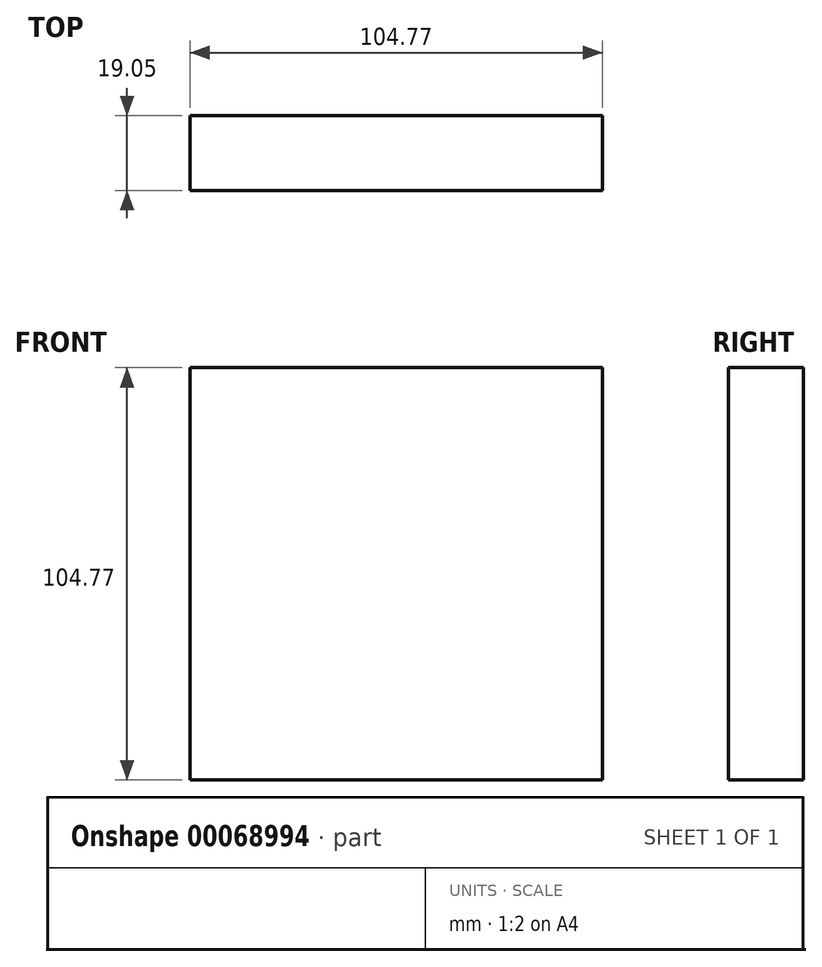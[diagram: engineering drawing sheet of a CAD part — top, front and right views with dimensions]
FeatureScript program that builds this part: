
annotation { "Feature Type Name" : "Feature", "Feature Type Description" : "" }
export const myFeature = defineFeature(function(context is Context, id is Id, definition is map)
    precondition{}
    {
        {
            var Q0;
            Q0=qCreatedBy(makeId("Front.planeOp"),FACE);
            var sketch = newSketch(context, id + "F0", { "sketchPlane" : qUnion([Q0])});
            skLineSegment(sketch, "E0.bottom", {"start": v(0, 0) * mm, "end": v(104.77, 0) * mm});
            skLineSegment(sketch, "E0.top", {"start": v(0, 104.78) * mm, "end": v(104.77, 104.78) * mm});
            skLineSegment(sketch, "E0.left", {"start": v(0, 0) * mm, "end": v(0, 104.78) * mm});
            skLineSegment(sketch, "E0.right", {"start": v(104.77, 0) * mm, "end": v(104.77, 104.78) * mm});
            skSolve(sketch);
        }
        {
            var Q0;
            Q0=makeQuery(id+"F0.imprint","IMPRINT",FACE,{"disambiguationData":[TD([[makeQuery(id+"F0.imprint","IMPRINT",EDGE,{"derivedFrom":sQuery(id+"F0.wireOp",EDGE,"E0.bottom")}),1.0]])]});
            extrude(context, id + "F1", {"entities" : qUnion([Q0]), "depth" : 19.05 * mm});
        }
    });
